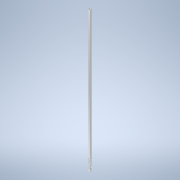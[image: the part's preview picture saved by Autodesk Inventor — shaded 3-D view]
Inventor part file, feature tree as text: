
AUTODESK INVENTOR PART (.ipt)
format: ipt  version: 2020.3 (Build 243373000, 373)  size: 191,488 bytes
history: native  units: mm
features: sketch x7, hole x6, other x1, extrude x1
ambient origin geometry x8: Origin, YZ Plane, XZ Plane, XY Plane, X Axis, Y Axis, Z Axis, Center Point
bodies: Body1 (feature_tree)
feature tree (15):
  other  "ソリッド1"
  extrude  "押し出し1"  Depth=15.0mm
  hole  "穴1"  [1 undecoded]
  hole  "穴2"  [1 undecoded]
  hole  "穴3"  [1 undecoded]
  hole  "穴4"  [1 undecoded]
  hole  "穴5"  [1 undecoded]
  hole  "穴6"  [1 undecoded]
  sketch  "スケッチ1"
  sketch  "スケッチ3"
  sketch  "スケッチ4"
  sketch  "スケッチ5"
  sketch  "スケッチ6"
  sketch  "スケッチ7"
  sketch  "スケッチ8"
note: 6 required parameter values undecoded (feature->parameter linkage not recoverable at this tier; creation-order binding heuristic only, values carry confidence <= 0.55)
